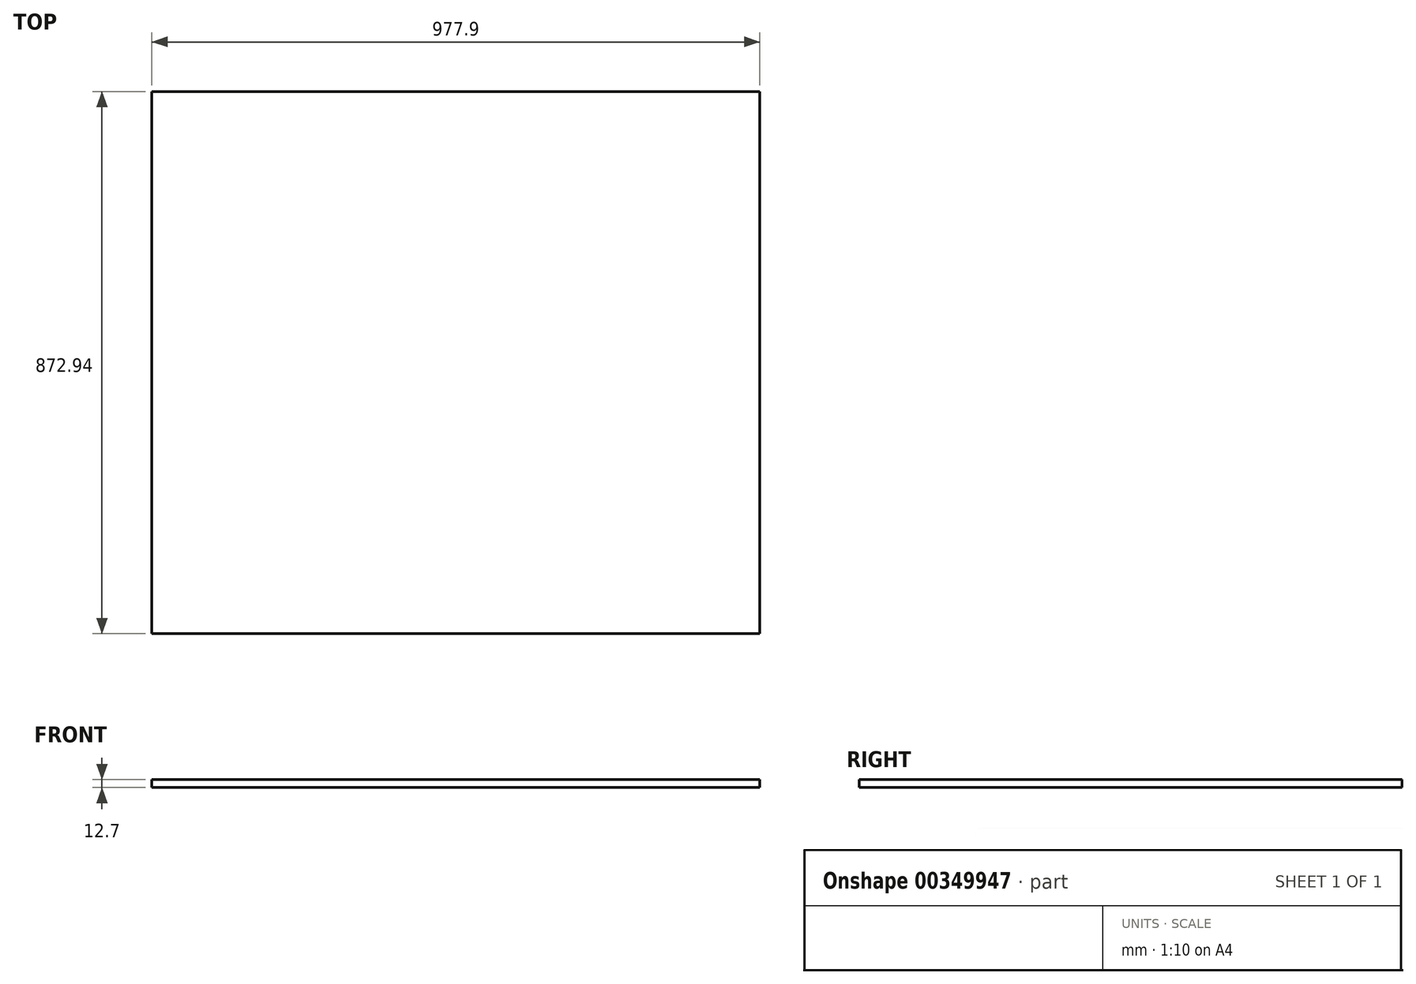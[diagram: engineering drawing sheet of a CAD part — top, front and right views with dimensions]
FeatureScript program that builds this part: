
annotation { "Feature Type Name" : "Feature", "Feature Type Description" : "" }
export const myFeature = defineFeature(function(context is Context, id is Id, definition is map)
    precondition{}
    {
        {
            var Q0;
            Q0=qCreatedBy(makeId("Top.planeOp"),FACE);
            var sketch = newSketch(context, id + "F0", { "sketchPlane" : qUnion([Q0])});
            skLineSegment(sketch, "E0.bottom", {"start": v(488.95, -436.47) * mm, "end": v(-488.95, -436.47) * mm});
            skLineSegment(sketch, "E0.top", {"start": v(488.95, 436.47) * mm, "end": v(-488.95, 436.47) * mm});
            skLineSegment(sketch, "E0.left", {"start": v(488.95, -436.47) * mm, "end": v(488.95, 436.47) * mm});
            skLineSegment(sketch, "E0.right", {"start": v(-488.95, -436.47) * mm, "end": v(-488.95, 436.47) * mm});
            skPoint(sketch, "E0.middle", {"position": v(0, 0) * mm});
            skSolve(sketch);
        }
        {
            var Q0;
            Q0 = qSketchRegion(id + "F0", true);
            extrude(context, id + "F1", {"entities" : qUnion([Q0]), "depth" : 12.7 * mm, "offsetDistance" : 25.4 * mm});
        }
    });
